# Revit family: Regus Sensors_M30_RFA
name_source: partatom
category: Pipe Accessories
units: mm (PartAtom-declared; Revit-internal decimal feet)

## family parameters
Always vertical = Yes
Cut with Voids When Loaded = No
OmniClass Number = 23.65.55.14.17
OmniClass Title = Adjusting/Controlling Valves for Liquid Services
Part Type = Normal
Round Connector Dimension = Use Diameter
Shared = Yes
Work Plane-Based = No

## types (2) — shared parameters
Body Material = Danfoss Plastic White
Connection = M30 x 1.5
Description = Radiator Sensor
IfcExportAs = IfcActuatorType
IfcExportType = Regus Sensors
Manufacturer = Danfoss
Max Temperature Setting = 28 °C
Sensor Media = Liquid
URL = https://store.danfoss.com

## per-type parameters (varying)
| type | Min Temperature Setting | Model | Model Type |
| Regus Sensors_M30_Built-in_8-28 °C | 8 °C | 015G3630,015G3839,015G5312 | Regus Sensors_M30_Built-in_8-28 °C |
| Regus Sensors_M30_Built-in_16-28 °C_015G3636 | 16 °C | 015G3636 | Regus Sensors_M30_Built-in_16-28 °C |

## geometry (parser evidence)
native form markers: Blend x4, Sweep x1
no freeform markers — native parametric forms only
